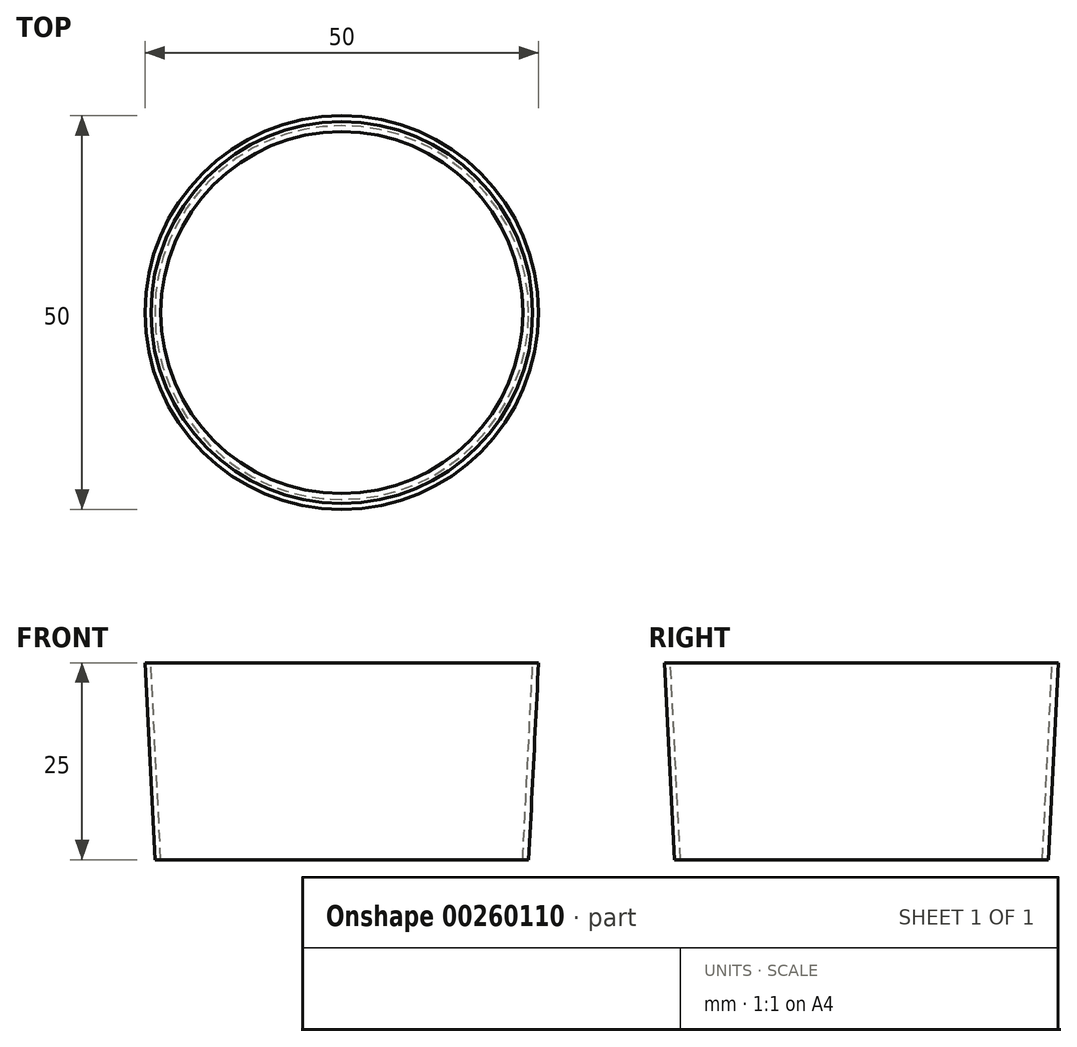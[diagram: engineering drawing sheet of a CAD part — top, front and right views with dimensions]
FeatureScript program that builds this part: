
annotation { "Feature Type Name" : "Feature", "Feature Type Description" : "" }
export const myFeature = defineFeature(function(context is Context, id is Id, definition is map)
    precondition{}
    {
        {
            var Q0;
            Q0=qCreatedBy(makeId("Top.planeOp"),FACE);
            var sketch = newSketch(context, id + "F0", { "sketchPlane" : qUnion([Q0])});
            skCircle(sketch, "E0", {"center": v(0, 0) * mm, "radius": 25 * mm});
            skSolve(sketch);
        }
        {
            var Q0;
            Q0 = qSketchRegion(id + "F0", true);
            extrude(context, id + "F1", {"entities" : qUnion([Q0]), "oppositeDirection" : true, "depth" : 25 * mm, "hasDraft" : true, "draftAngle" : 2.87 * degree, "draftPullDirection" : true});
        }
        {
            var Q0;
            Q0=makeQuery(id+"F1.opExtrude","CAP_FACE",FACE,{"disambiguationData":[OSD([sQuery(id+"F0.wireOp",EDGE,"E0")])],"isStart":true});
            var Q1;
            Q1=makeQuery(id+"F1.opExtrude","CAP_FACE",FACE,{"disambiguationData":[OSD([sQuery(id+"F0.wireOp",EDGE,"E0")])],"isStart":false});
            shell(context, id + "F2", {"entities" : qUnion([Q0, Q1]), "thickness" : 0.75 * mm});
        }
    });
